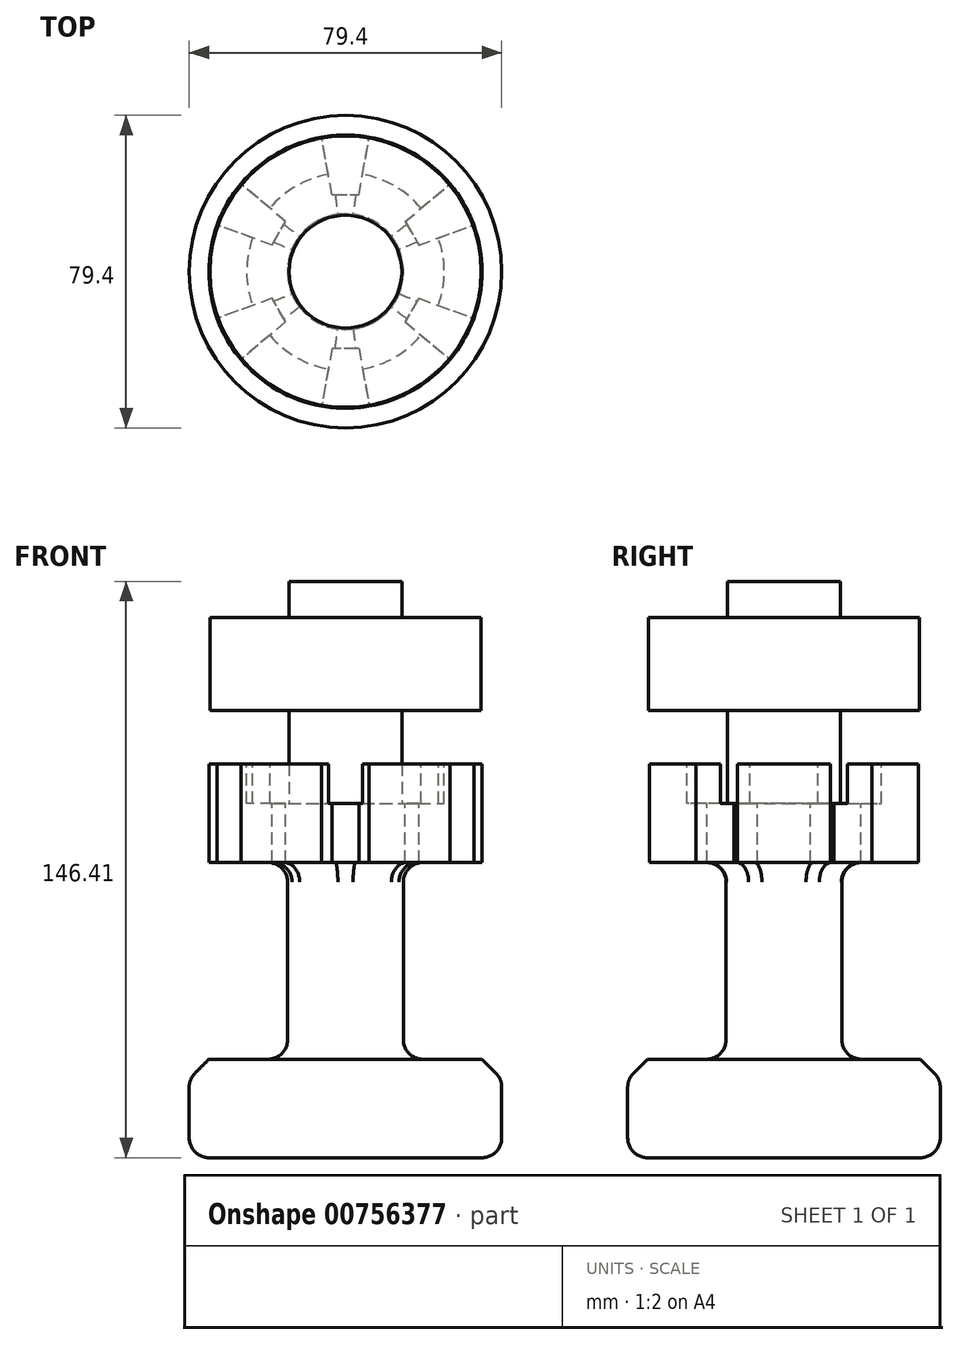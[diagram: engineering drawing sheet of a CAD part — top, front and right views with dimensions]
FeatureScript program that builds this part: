
annotation { "Feature Type Name" : "Feature", "Feature Type Description" : "" }
export const myFeature = defineFeature(function(context is Context, id is Id, definition is map)
    precondition{}
    {
        {
            var Q0;
            Q0=qCreatedBy(makeId("Front.planeOp"),FACE);
            var sketch = newSketch(context, id + "F0", { "sketchPlane" : qUnion([Q0])});
            skLineSegment(sketch, "E0.bottom", {"start": v(0, 0) * mm, "end": v(39.7, 0) * mm});
            skLineSegment(sketch, "E0.top", {"start": v(14.7, 25) * mm, "end": v(39.7, 25) * mm});
            skLineSegment(sketch, "E0.left", {"start": v(0, 0) * mm, "end": v(0, 25) * mm});
            skLineSegment(sketch, "E0.right", {"start": v(39.7, 0) * mm, "end": v(39.7, 25) * mm});
            skLineSegment(sketch, "E1.bottom", {"start": v(0, 0) * mm, "end": v(14.7, 0) * mm});
            skLineSegment(sketch, "E1.left", {"start": v(0, 0) * mm, "end": v(0, 75) * mm});
            skLineSegment(sketch, "E1.right", {"start": v(14.7, 25) * mm, "end": v(14.7, 75) * mm});
            skLineSegment(sketch, "E2.bottom", {"start": v(14.7, 75) * mm, "end": v(34.7, 75) * mm});
            skLineSegment(sketch, "E2.top", {"start": v(14.31, 100) * mm, "end": v(34.7, 100) * mm});
            skLineSegment(sketch, "E2.left", {"start": v(0, 75) * mm, "end": v(0, 100) * mm});
            skLineSegment(sketch, "E2.right", {"start": v(34.7, 75) * mm, "end": v(34.7, 100) * mm});
            skLineSegment(sketch, "E3.bottom", {"start": v(14.31, 100) * mm, "end": v(14.75, 100) * mm});
            skLineSegment(sketch, "E4.top", {"start": v(0, 146.4) * mm, "end": v(14.31, 146.4) * mm});
            skLineSegment(sketch, "E4.left", {"start": v(0, 100) * mm, "end": v(0, 146.4) * mm});
            skLineSegment(sketch, "E4.right", {"start": v(14.31, 100) * mm, "end": v(14.31, 114.06) * mm});
            skLineSegment(sketch, "E5.trimOffspring", {"start": v(14.31, 137.22) * mm, "end": v(14.31, 146.4) * mm});
            skLineSegment(sketch, "E6.bottom", {"start": v(14.31, 137.22) * mm, "end": v(34.45, 137.22) * mm});
            skLineSegment(sketch, "E6.top", {"start": v(14.31, 113.65) * mm, "end": v(34.45, 113.65) * mm});
            skLineSegment(sketch, "E6.left", {"start": v(14.31, 114.06) * mm, "end": v(14.31, 113.65) * mm});
            skLineSegment(sketch, "E6.right", {"start": v(34.45, 137.22) * mm, "end": v(34.45, 113.65) * mm});
            skSolve(sketch);
        }
        {
            var Q0;
            Q0=makeQuery(id+"F0.imprint","IMPRINT",FACE,{"disambiguationData":[TD([[makeQuery(id+"F0.imprint","IMPRINT",EDGE,{"derivedFrom":sQuery(id+"F0.wireOp",EDGE,"E0.bottom")}),1.0]])]});
            var Q1;
            Q1=sQuery(id+"F0.wireOp",EDGE,"E1.left");
            revolve(context, id + "F1", {"surfaceOperationType" : NewSurfaceOperationType.NEW, "entities" : qUnion([Q0]), "axis" : qUnion([Q1]), "revolveType" : RevolveType.FULL});
        }
        {
            var Q0;
            Q0=makeQuery(id+"F1.opRevolve","SWEPT_FACE",FACE,{"disambiguationData":[OSD([sQuery(id+"F0.wireOp",EDGE,"E2.top")])]});
            var sketch = newSketch(context, id + "F2", { "sketchPlane" : qUnion([Q0])});
            skPoint(sketch, "E7.middle", {"position": v(0, 0) * mm});
            skCircle(sketch, "E8", {"center": v(0, 0) * mm, "radius": 25.1 * mm});
            skSolve(sketch);
        }
        {
            var Q0;
            Q0=makeQuery(id+"F2.imprint","IMPRINT",FACE,{"disambiguationData":[TD([[makeQuery(id+"F2.imprint","IMPRINT",EDGE,{"derivedFrom":sQuery(id+"F2.wireOp",EDGE,"E8")}),1.0]])]});
            extrude(context, id + "F3", {"entities" : qUnion([Q0]), "operationType" : NewBodyOperationType.REMOVE, "endBound" : BoundingType.SYMMETRIC, "oppositeDirection" : true, "depth" : 20 * mm, "offsetDistance" : 25 * mm});
        }
        {
            var Q0;
            Q0=makeQuery(id+"F2.imprint","IMPRINT",FACE,{"disambiguationData":[TD([[makeQuery(id+"F2.imprint","IMPRINT",EDGE,{"derivedFrom":sQuery(id+"F2.wireOp",EDGE,"E8")}),-1.0]])]});
            var sketch = newSketch(context, id + "F4", { "sketchPlane" : qUnion([Q0])});
            skLineSegment(sketch, "E9", {"start": v(3.44, 19.53) * mm, "end": v(8.37, 47.46) * mm});
            skLineSegment(sketch, "E10", {"start": v(-3.44, 19.53) * mm, "end": v(-8.37, 47.46) * mm});
            skLineSegment(sketch, "E11", {"start": v(-8.37, 47.46) * mm, "end": v(8.37, 47.46) * mm});
            skLineSegment(sketch, "E12", {"start": v(-3.44, 19.53) * mm, "end": v(3.44, 19.53) * mm});
            skLineSegment(sketch, "E13.1.0", {"start": v(-18.63, 6.78) * mm, "end": v(-45.29, 16.48) * mm});
            skLineSegment(sketch, "E13.1.1", {"start": v(-45.29, 16.48) * mm, "end": v(-36.92, 30.98) * mm});
            skLineSegment(sketch, "E13.1.2", {"start": v(-15.19, 12.75) * mm, "end": v(-36.92, 30.98) * mm});
            skLineSegment(sketch, "E13.1.3", {"start": v(-18.63, 6.78) * mm, "end": v(-15.19, 12.75) * mm});
            skLineSegment(sketch, "E13.2.0", {"start": v(-15.19, -12.75) * mm, "end": v(-36.92, -30.98) * mm});
            skLineSegment(sketch, "E13.2.1", {"start": v(-36.92, -30.98) * mm, "end": v(-45.29, -16.48) * mm});
            skLineSegment(sketch, "E13.2.2", {"start": v(-18.63, -6.78) * mm, "end": v(-45.29, -16.48) * mm});
            skLineSegment(sketch, "E13.2.3", {"start": v(-15.19, -12.75) * mm, "end": v(-18.63, -6.78) * mm});
            skLineSegment(sketch, "E13.3.0", {"start": v(3.44, -19.53) * mm, "end": v(8.37, -47.46) * mm});
            skLineSegment(sketch, "E13.3.1", {"start": v(8.37, -47.46) * mm, "end": v(-8.37, -47.46) * mm});
            skLineSegment(sketch, "E13.3.2", {"start": v(-3.44, -19.53) * mm, "end": v(-8.37, -47.46) * mm});
            skLineSegment(sketch, "E13.3.3", {"start": v(3.44, -19.53) * mm, "end": v(-3.44, -19.53) * mm});
            skLineSegment(sketch, "E13.4.0", {"start": v(18.63, -6.78) * mm, "end": v(45.29, -16.48) * mm});
            skLineSegment(sketch, "E13.4.1", {"start": v(45.29, -16.48) * mm, "end": v(36.92, -30.98) * mm});
            skLineSegment(sketch, "E13.4.2", {"start": v(15.19, -12.75) * mm, "end": v(36.92, -30.98) * mm});
            skLineSegment(sketch, "E13.4.3", {"start": v(18.63, -6.78) * mm, "end": v(15.19, -12.75) * mm});
            skLineSegment(sketch, "E13.5.0", {"start": v(15.19, 12.75) * mm, "end": v(36.92, 30.98) * mm});
            skLineSegment(sketch, "E13.5.1", {"start": v(36.92, 30.98) * mm, "end": v(45.29, 16.48) * mm});
            skLineSegment(sketch, "E13.5.2", {"start": v(18.63, 6.78) * mm, "end": v(45.29, 16.48) * mm});
            skLineSegment(sketch, "E13.5.3", {"start": v(15.19, 12.75) * mm, "end": v(18.63, 6.78) * mm});
            skPoint(sketch, "E13.center", {"position": v(0, 0) * mm});
            skSolve(sketch);
        }
        {
            var Q0;
            Q0 = qSketchRegion(id + "F4", true);
            extrude(context, id + "F5", {"entities" : qUnion([Q0]), "operationType" : NewBodyOperationType.REMOVE, "oppositeDirection" : true, "depth" : 25 * mm, "offsetDistance" : 25 * mm});
        }
        {
            var Q0;
            Q0=makeQuery(id+"F1.opRevolve","SWEPT_EDGE",EDGE,{"disambiguationData":[OSD([sQuery(id+"F0.wireOp",EDGE,"E0.top"),sQuery(id+"F0.wireOp",EDGE,"E0.right")])]});
            chamfer(context, id + "F6", {"entities" : qUnion([Q0]), "width" : 5 * mm, "tangentPropagation" : true});
        }
        {
            var Q0;
            Q0=makeQuery(id+"F1.opRevolve","SWEPT_FACE",FACE,{"disambiguationData":[OSD([sQuery(id+"F0.wireOp",EDGE,"E0.right")])]});
            var Q1;
            Q1=makeQuery(id+"F1.opRevolve","SWEPT_FACE",FACE,{"disambiguationData":[OSD([sQuery(id+"F0.wireOp",EDGE,"E1.right")])]});
            fillet(context, id + "F7", {"entities" : qUnion([Q0, Q1]), "radius" : 5 * mm, "tangentPropagation" : true, "allowEdgeOverflow" : false});
        }
    });
